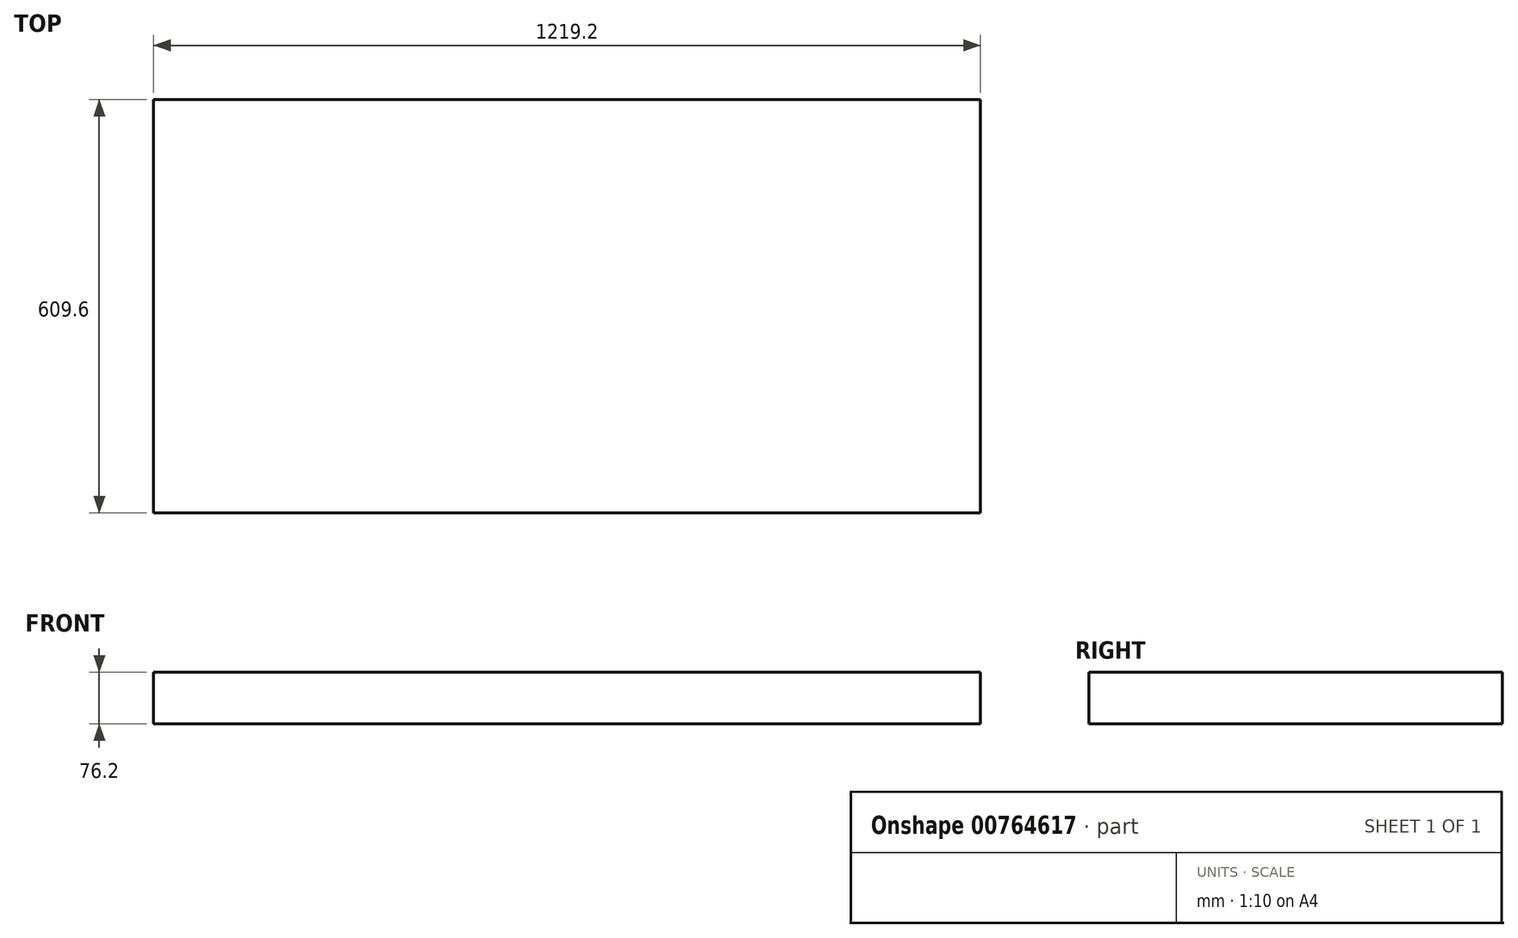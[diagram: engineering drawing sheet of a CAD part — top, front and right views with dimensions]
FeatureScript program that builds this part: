
annotation { "Feature Type Name" : "Feature", "Feature Type Description" : "" }
export const myFeature = defineFeature(function(context is Context, id is Id, definition is map)
    precondition{}
    {
        {
            var Q0;
            Q0=qCreatedBy(makeId("Top.planeOp"),FACE);
            var sketch = newSketch(context, id + "F0", { "sketchPlane" : qUnion([Q0])});
            skLineSegment(sketch, "E0.bottom", {"start": v(0, 0) * mm, "end": v(-1219.2, 0) * mm});
            skLineSegment(sketch, "E0.top", {"start": v(0, 609.6) * mm, "end": v(-1219.2, 609.6) * mm});
            skLineSegment(sketch, "E0.left", {"start": v(0, 0) * mm, "end": v(0, 609.6) * mm});
            skLineSegment(sketch, "E0.right", {"start": v(-1219.2, 0) * mm, "end": v(-1219.2, 609.6) * mm});
            skSolve(sketch);
        }
        {
            var Q0;
            Q0=makeQuery(id+"F0.imprint","IMPRINT",FACE,{"disambiguationData":[TD([[makeQuery(id+"F0.imprint","IMPRINT",EDGE,{"derivedFrom":sQuery(id+"F0.wireOp",EDGE,"E0.bottom")}),-1.0]])]});
            extrude(context, id + "F1", {"entities" : qUnion([Q0]), "depth" : 76.2 * mm, "offsetDistance" : 25.4 * mm});
        }
    });
